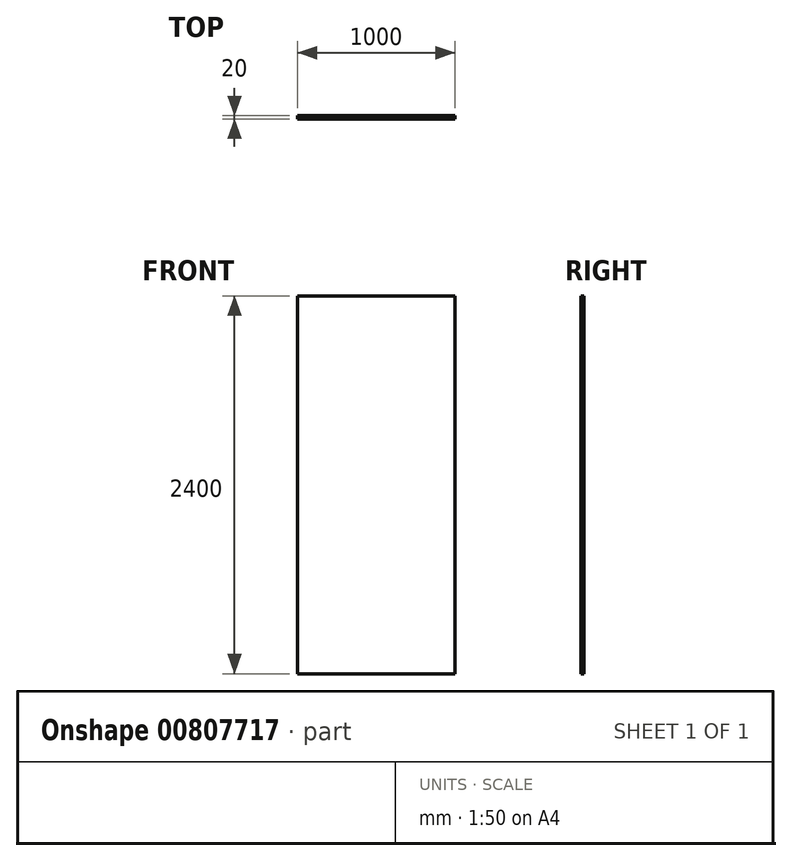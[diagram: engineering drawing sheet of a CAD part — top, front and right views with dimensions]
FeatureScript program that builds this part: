
annotation { "Feature Type Name" : "Feature", "Feature Type Description" : "" }
export const myFeature = defineFeature(function(context is Context, id is Id, definition is map)
    precondition{}
    {
        {
            var Q0;
            Q0=qCreatedBy(makeId("Front.planeOp"),FACE);
            var sketch = newSketch(context, id + "F0", { "sketchPlane" : qUnion([Q0])});
            skLineSegment(sketch, "E0.bottom", {"start": v(-594.24, 1599.2) * mm, "end": v(405.76, 1599.2) * mm});
            skLineSegment(sketch, "E0.top", {"start": v(-594.24, -800.8) * mm, "end": v(405.76, -800.8) * mm});
            skLineSegment(sketch, "E0.left", {"start": v(-594.24, 1599.2) * mm, "end": v(-594.24, -800.8) * mm});
            skLineSegment(sketch, "E0.right", {"start": v(405.76, 1599.2) * mm, "end": v(405.76, -800.8) * mm});
            skSolve(sketch);
        }
        {
            var Q0;
            Q0=makeQuery(id+"F0.imprint","IMPRINT",FACE,{"disambiguationData":[TD([[makeQuery(id+"F0.imprint","IMPRINT",EDGE,{"derivedFrom":sQuery(id+"F0.wireOp",EDGE,"E0.bottom")}),-1.0]])]});
            extrude(context, id + "F1", {"entities" : qUnion([Q0]), "endBound" : BoundingType.SYMMETRIC, "depth" : 20 * mm, "offsetDistance" : 25 * mm});
        }
    });
